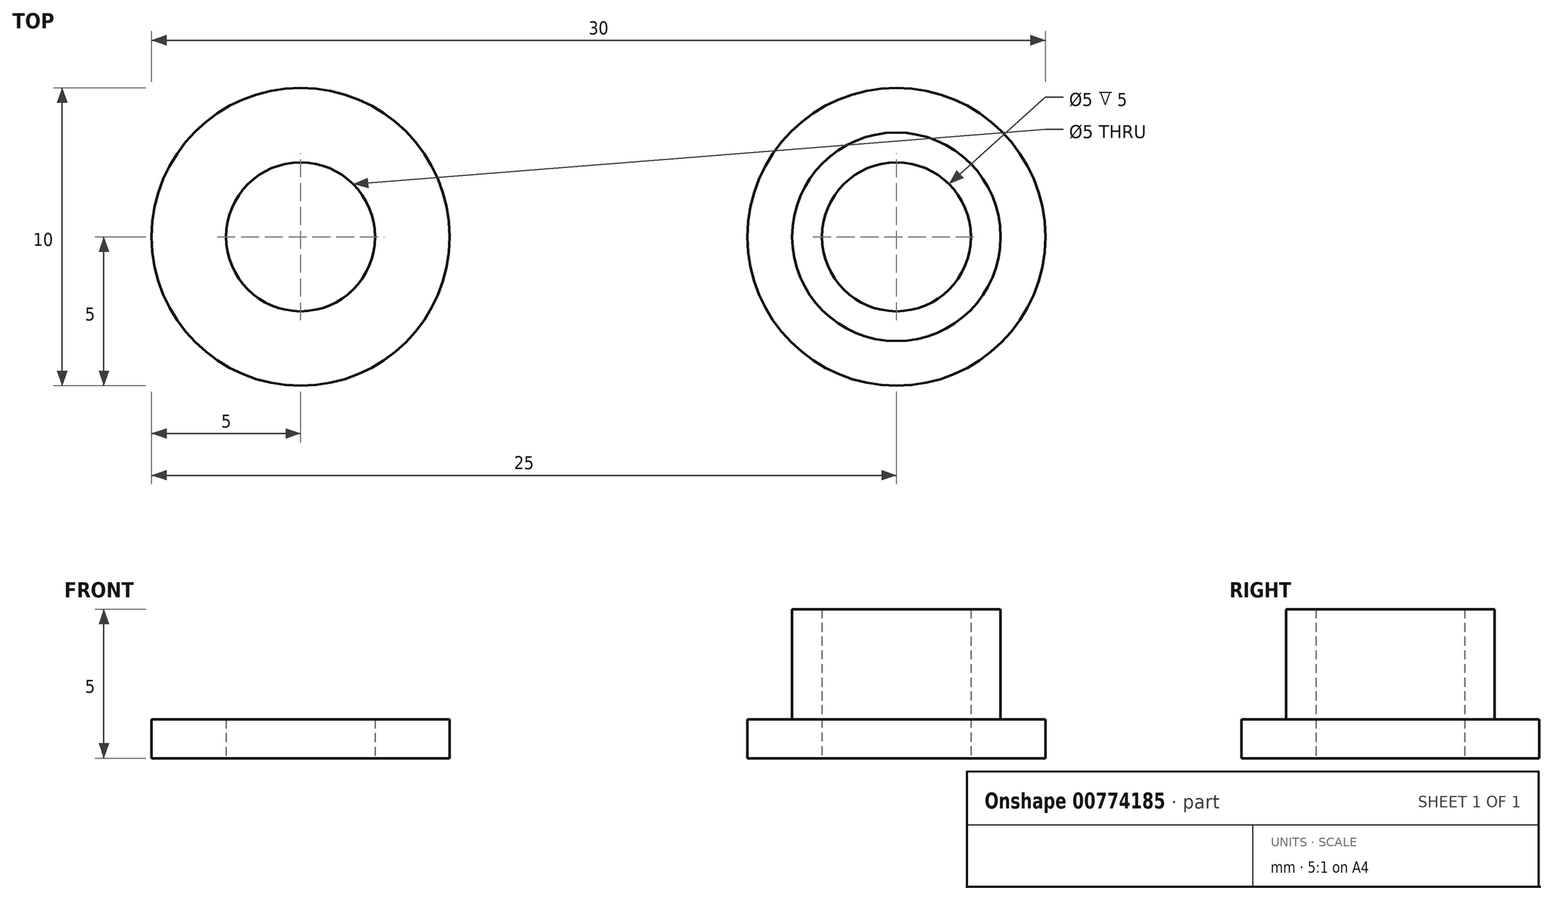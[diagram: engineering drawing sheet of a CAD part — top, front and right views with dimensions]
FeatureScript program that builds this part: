
annotation { "Feature Type Name" : "Feature", "Feature Type Description" : "" }
export const myFeature = defineFeature(function(context is Context, id is Id, definition is map)
    precondition{}
    {
        {
            var Q0;
            Q0=qCreatedBy(makeId("Top.planeOp"),FACE);
            var sketch = newSketch(context, id + "F0", { "sketchPlane" : qUnion([Q0])});
            skCircle(sketch, "E0", {"center": v(0, 0) * mm, "radius": 2.5 * mm});
            skCircle(sketch, "E1", {"center": v(0, 0) * mm, "radius": 3.5 * mm});
            skSolve(sketch);
        }
        {
            var Q0;
            Q0 = qSketchRegion(id + "F0", true);
            extrude(context, id + "F1", {"entities" : qUnion([Q0]), "depth" : 5 * mm, "offsetDistance" : 25 * mm});
        }
        {
            var Q0;
            Q0=qCreatedBy(makeId("Top.planeOp"),FACE);
            var sketch = newSketch(context, id + "F2", { "sketchPlane" : qUnion([Q0])});
            skCircle(sketch, "E2", {"center": v(0, 0) * mm, "radius": 2.5 * mm});
            skCircle(sketch, "E3", {"center": v(0, 0) * mm, "radius": 5 * mm});
            skSolve(sketch);
        }
        {
            var Q0;
            Q0 = qSketchRegion(id + "F2", true);
            extrude(context, id + "F3", {"entities" : qUnion([Q0]), "operationType" : NewBodyOperationType.ADD, "depth" : 1.3 * mm, "offsetDistance" : 25 * mm});
        }
        {
            var Q0;
            Q0=makeQuery(id+"F1.opExtrude","SWEPT_BODY",BODY,{"disambiguationData":[OSD([sQuery(id+"F0.wireOp",EDGE,"E0"),sQuery(id+"F0.wireOp",EDGE,"E1")])]});
            transform(context, id + "F4", {"entities" : qUnion([Q0]), "transformType" : TransformType.TRANSLATION_3D, "dx" : 20 * mm, "dy" : 0 * mm, "dz" : 0 * mm, "makeCopy" : false});
        }
        {
            var Q0;
            Q0=qCreatedBy(makeId("Top.planeOp"),FACE);
            var sketch = newSketch(context, id + "F5", { "sketchPlane" : qUnion([Q0])});
            skCircle(sketch, "E4", {"center": v(0, 0) * mm, "radius": 2.5 * mm});
            skCircle(sketch, "E5", {"center": v(0, 0) * mm, "radius": 5 * mm});
            skSolve(sketch);
        }
        {
            var Q0;
            Q0 = qSketchRegion(id + "F5", true);
            extrude(context, id + "F6", {"entities" : qUnion([Q0]), "depth" : 1.3 * mm, "offsetDistance" : 25 * mm});
        }
    });
